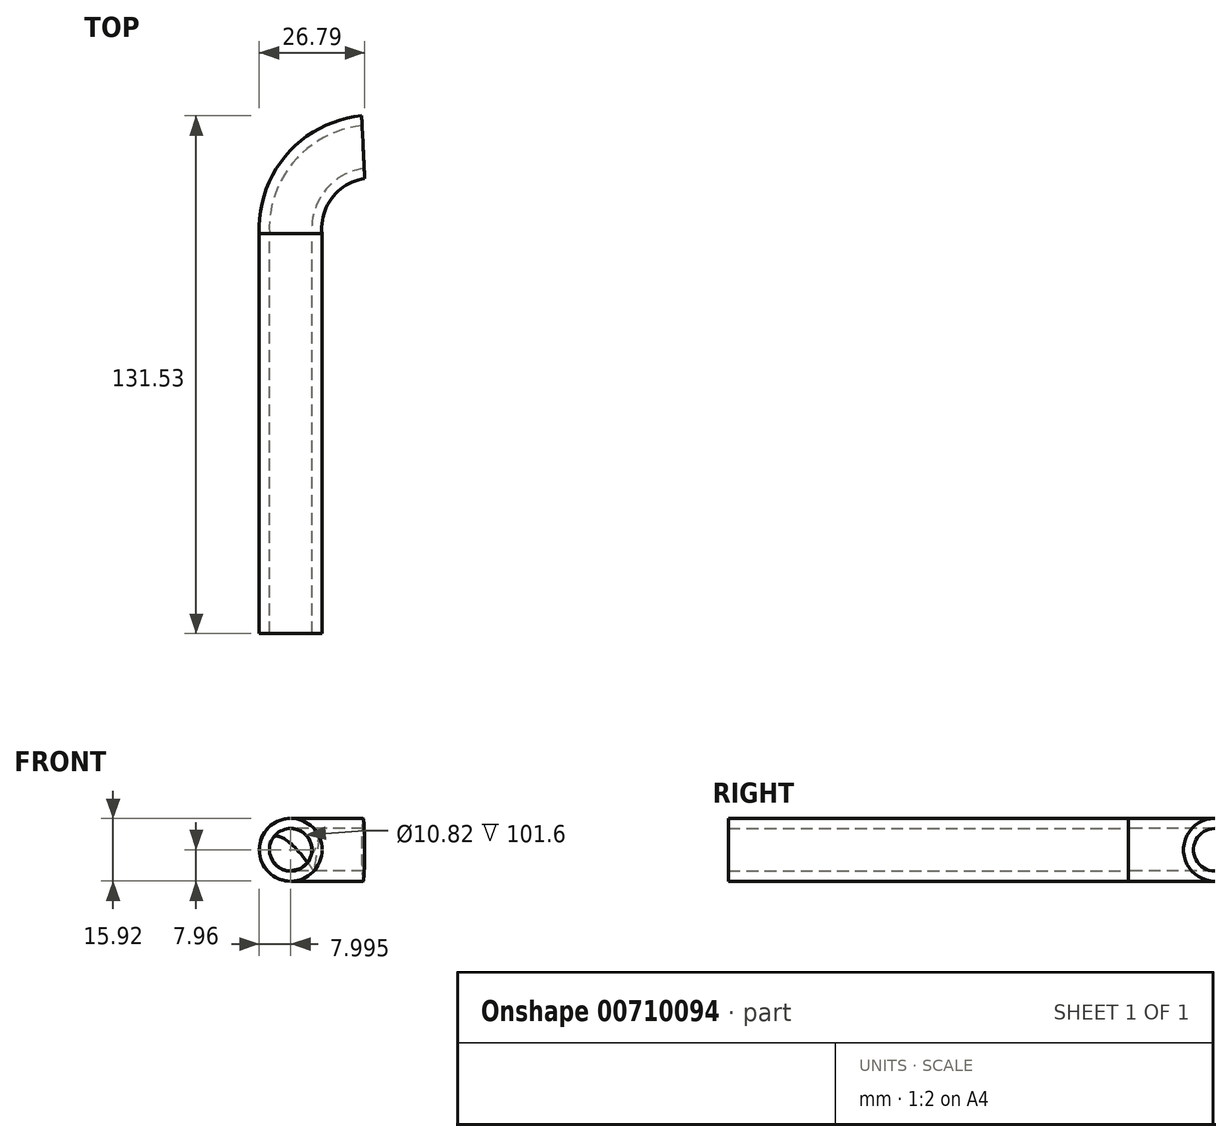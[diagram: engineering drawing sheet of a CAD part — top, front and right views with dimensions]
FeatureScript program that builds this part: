
annotation { "Feature Type Name" : "Feature", "Feature Type Description" : "" }
export const myFeature = defineFeature(function(context is Context, id is Id, definition is map)
    precondition{}
    {
        {
            var Q0;
            Q0=qCreatedBy(makeId("Top.planeOp"),FACE);
            var sketch = newSketch(context, id + "F0", { "sketchPlane" : qUnion([Q0])});
            skLineSegment(sketch, "E0", {"start": v(-37.36, -74.88) * mm, "end": v(-37.36, 26.72) * mm});
            skArc(sketch, "E1", {"start": v(-37.36, 26.72) * mm, "mid": v(-31.64, 41.03) * mm, "end": v(-17.63, 47.44) * mm});
            skSolve(sketch);
        }
        {
            var Q0;
            Q0=qCreatedBy(makeId("Front.planeOp"),FACE);
            cPlane(context, id + "F1", {"entities" : qUnion([Q0]), "cplaneType" : CPlaneType.OFFSET, "offset" : 76.2 * mm, "width" : 152.4 * mm, "height" : 152.4 * mm});
        }
        {
            var Q0;
            Q0=qCreatedBy(id+"F1.planeOp",FACE);
            var sketch = newSketch(context, id + "F2", { "sketchPlane" : qUnion([Q0])});
            skPoint(sketch, "E2.0", {"position": v(-37.36, 0) * mm});
            skCircle(sketch, "E3", {"center": v(-37.36, 0) * mm, "radius": 7.96 * mm});
            skCircle(sketch, "E4", {"center": v(-37.36, 0) * mm, "radius": 5.41 * mm});
            skSolve(sketch);
        }
        {
            var Q0;
            Q0=makeQuery(id+"F2.imprint","IMPRINT",FACE,{"disambiguationData":[TD([[makeQuery(id+"F2.imprint","IMPRINT",EDGE,{"derivedFrom":sQuery(id+"F2.wireOp",EDGE,"E3")}),1.0]])]});
            var Q1;
            Q1=sQuery(id+"F0.wireOp",EDGE,"E0");
            var Q2;
            Q2=sQuery(id+"F0.wireOp",EDGE,"E1");
            sweep(context, id + "F3", {"profiles" : qUnion([Q0]), "path" : qUnion([Q1, Q2])});
        }
    });
